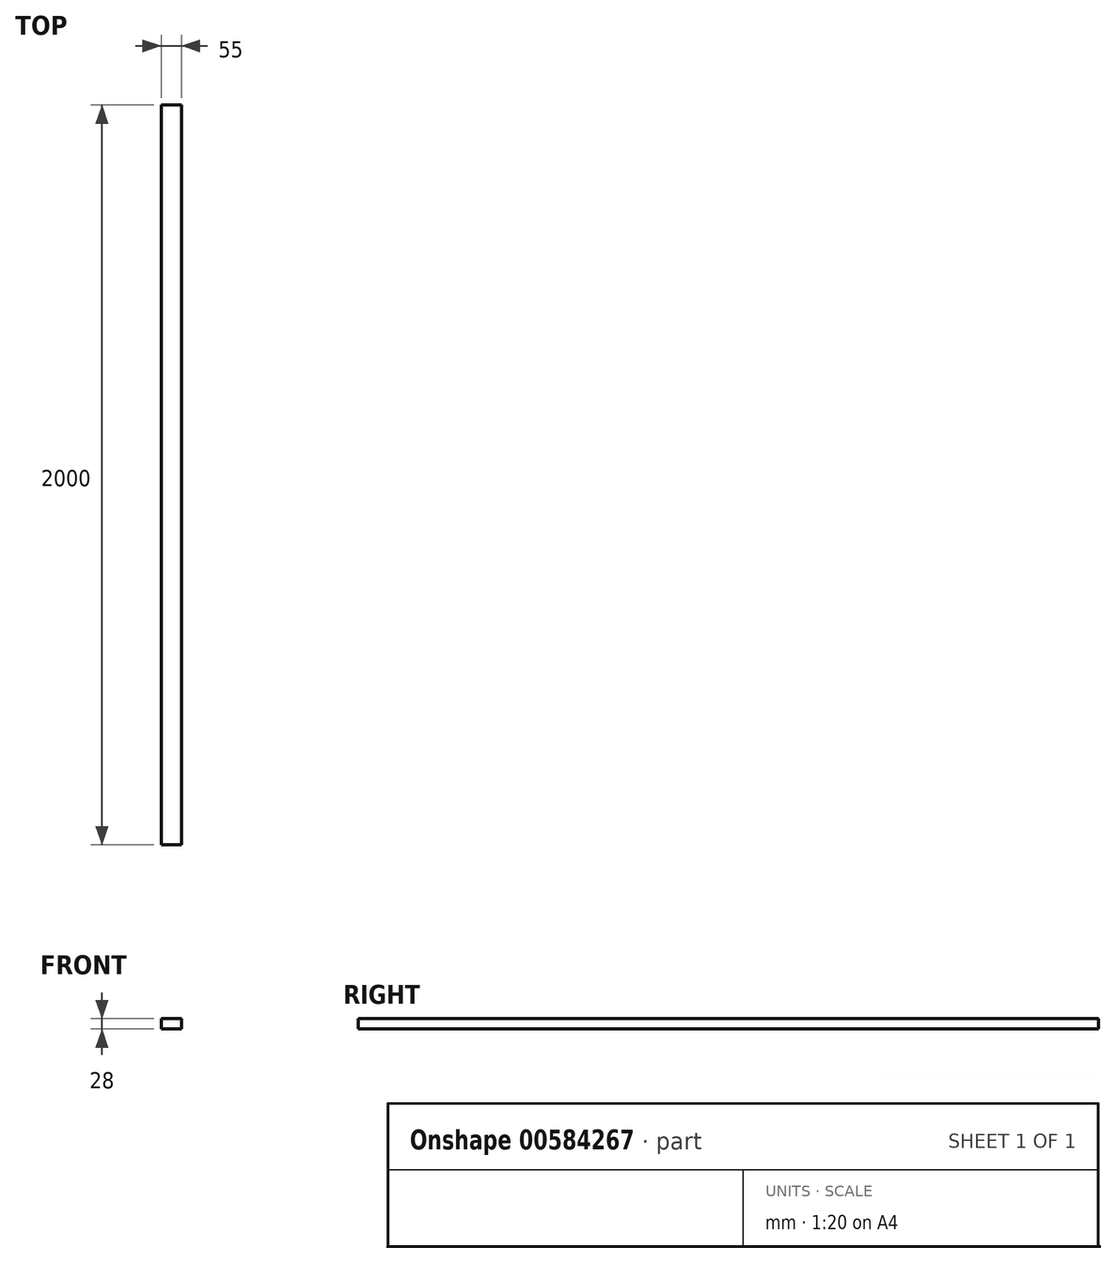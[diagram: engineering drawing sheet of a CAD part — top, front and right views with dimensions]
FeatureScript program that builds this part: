
annotation { "Feature Type Name" : "Feature", "Feature Type Description" : "" }
export const myFeature = defineFeature(function(context is Context, id is Id, definition is map)
    precondition{}
    {
        {
            var Q0;
            Q0=qCreatedBy(makeId("Front.planeOp"),FACE);
            var sketch = newSketch(context, id + "F0", { "sketchPlane" : qUnion([Q0])});
            skLineSegment(sketch, "E0.bottom", {"start": v(0, 0) * mm, "end": v(55, 0) * mm});
            skLineSegment(sketch, "E0.top", {"start": v(0, 28) * mm, "end": v(55, 28) * mm});
            skLineSegment(sketch, "E0.left", {"start": v(0, 0) * mm, "end": v(0, 28) * mm});
            skLineSegment(sketch, "E0.right", {"start": v(55, 0) * mm, "end": v(55, 28) * mm});
            skSolve(sketch);
        }
        {
            var Q0;
            Q0=makeQuery(id+"F0.imprint","IMPRINT",FACE,{"disambiguationData":[TD([[makeQuery(id+"F0.imprint","IMPRINT",EDGE,{"derivedFrom":sQuery(id+"F0.wireOp",EDGE,"E0.bottom")}),1.0]])]});
            extrude(context, id + "F1", {"entities" : qUnion([Q0]), "depth" : 2000 * mm, "offsetDistance" : 25 * mm});
        }
    });
